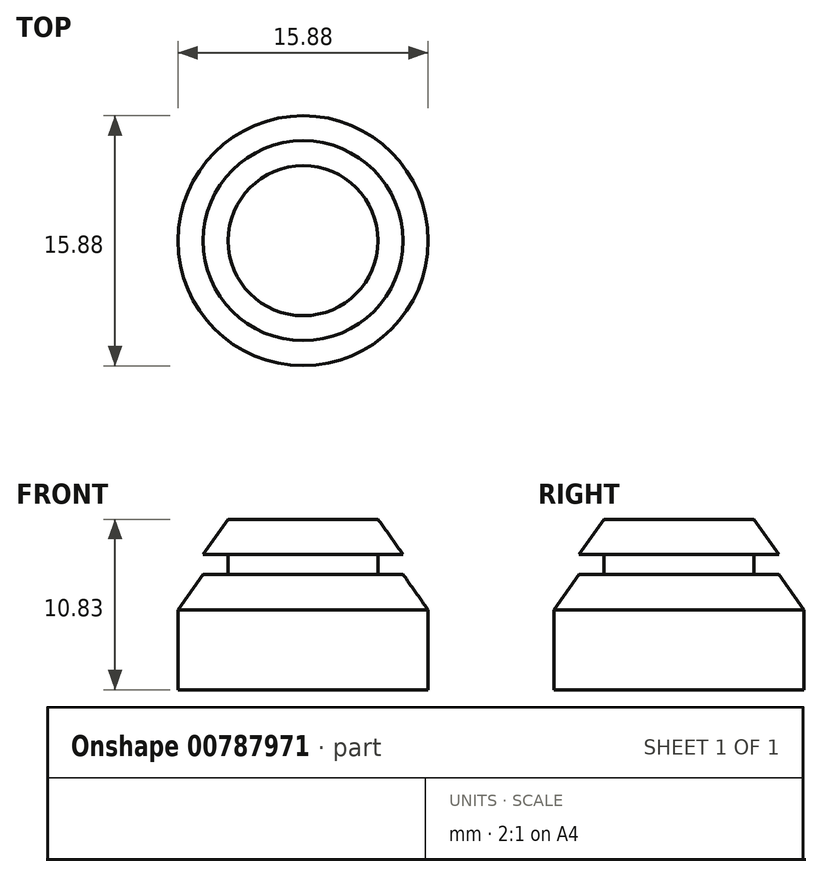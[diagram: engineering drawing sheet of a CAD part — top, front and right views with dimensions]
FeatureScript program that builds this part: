
annotation { "Feature Type Name" : "Feature", "Feature Type Description" : "" }
export const myFeature = defineFeature(function(context is Context, id is Id, definition is map)
    precondition{}
    {
        {
            var Q0;
            Q0=qCreatedBy(makeId("Front.planeOp"),FACE);
            var sketch = newSketch(context, id + "F0", { "sketchPlane" : qUnion([Q0])});
            skLineSegment(sketch, "E0", {"start": v(0, 0) * mm, "end": v(6.35, 0) * mm, "construction": true});
            skLineSegment(sketch, "E1", {"start": v(0, 0) * mm, "end": v(0, 2.24) * mm, "construction": true});
            skLineSegment(sketch, "E2", {"start": v(0, 2.24) * mm, "end": v(4.76, 2.24) * mm, "construction": true});
            skLineSegment(sketch, "E3", {"start": v(4.76, 2.24) * mm, "end": v(6.35, 0) * mm, "construction": true});
            skLineSegment(sketch, "E4", {"start": v(4.76, 0) * mm, "end": v(4.76, -1.27) * mm, "construction": true});
            skLineSegment(sketch, "E5", {"start": v(4.76, -1.27) * mm, "end": v(0, -1.27) * mm, "construction": true});
            skLineSegment(sketch, "E6", {"start": v(0, -1.27) * mm, "end": v(0, 0) * mm, "construction": true});
            skLineSegment(sketch, "E7", {"start": v(0, -1.27) * mm, "end": v(0, -3.51) * mm, "construction": true});
            skLineSegment(sketch, "E8", {"start": v(0, -3.51) * mm, "end": v(7.94, -3.51) * mm, "construction": true});
            skLineSegment(sketch, "E9", {"start": v(4.76, -1.27) * mm, "end": v(6.35, -1.27) * mm});
            skLineSegment(sketch, "E10", {"start": v(6.35, -1.27) * mm, "end": v(7.94, -3.51) * mm});
            skLineSegment(sketch, "E11", {"start": v(0, 2.24) * mm, "end": v(0, -3.51) * mm});
            skLineSegment(sketch, "E12", {"start": v(4.76, -1.27) * mm, "end": v(4.76, 0) * mm});
            skLineSegment(sketch, "E13", {"start": v(4.76, 0) * mm, "end": v(6.35, 0) * mm});
            skLineSegment(sketch, "E14", {"start": v(6.35, 0) * mm, "end": v(4.76, 2.24) * mm});
            skLineSegment(sketch, "E15", {"start": v(4.76, 2.24) * mm, "end": v(0, 2.24) * mm});
            skLineSegment(sketch, "E16", {"start": v(0, 3.69) * mm, "end": v(0, -4.74) * mm, "construction": true});
            skLineSegment(sketch, "E17", {"start": v(4.76, -1.27) * mm, "end": v(4.76, -6.05) * mm, "construction": true});
            skLineSegment(sketch, "E18", {"start": v(4.76, -6.05) * mm, "end": v(7.94, -6.05) * mm, "construction": true});
            skLineSegment(sketch, "E19", {"start": v(7.94, -6.05) * mm, "end": v(7.94, -3.51) * mm, "construction": true});
            skLineSegment(sketch, "E20.bottom", {"start": v(7.94, -6.05) * mm, "end": v(2.86, -6.05) * mm, "construction": true});
            skLineSegment(sketch, "E20.top", {"start": v(7.94, -8.6) * mm, "end": v(2.86, -8.6) * mm, "construction": true});
            skLineSegment(sketch, "E20.left", {"start": v(7.94, -6.05) * mm, "end": v(7.94, -8.6) * mm, "construction": true});
            skLineSegment(sketch, "E20.right", {"start": v(2.86, -6.05) * mm, "end": v(2.86, -8.6) * mm, "construction": true});
            skLineSegment(sketch, "E21", {"start": v(2.86, -8.6) * mm, "end": v(7.94, -8.6) * mm});
            skLineSegment(sketch, "E22", {"start": v(7.94, -8.6) * mm, "end": v(7.94, -3.51) * mm});
            skLineSegment(sketch, "E23", {"start": v(0, -3.51) * mm, "end": v(0, -8.6) * mm});
            skLineSegment(sketch, "E24", {"start": v(0, -8.6) * mm, "end": v(2.86, -8.6) * mm});
            skSolve(sketch);
        }
        {
            var Q0;
            Q0 = qSketchRegion(id + "F0", true);
            var Q1;
            Q1=sQuery(id+"F0.wireOp",EDGE,"E16");
            revolve(context, id + "F1", {"surfaceOperationType" : NewSurfaceOperationType.NEW, "entities" : qUnion([Q0]), "axis" : qUnion([Q1]), "revolveType" : RevolveType.FULL});
        }
    });
